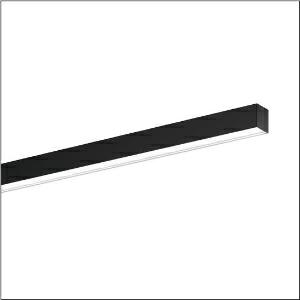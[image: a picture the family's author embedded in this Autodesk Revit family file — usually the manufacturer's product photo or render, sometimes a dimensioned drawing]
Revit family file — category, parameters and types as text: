
# Revit family: silica_r__21_51mx23tbt5b_7df7
name_source: partatom
category: Lighting Fixtures
units: mm (PartAtom-declared; Revit-internal decimal feet)

## family parameters
Cut with Voids When Loaded = No
Host = Face
Light Source = No
Part Type = Normal
Room Calculation Point = No
Round Connector Dimension = Use Diameter
Shared = No

## types (1)
- --- (1 x LED, 4030 lm, 40.5 W, 6500K)
    Apparent Load = 41 VA
    CIE Flux Codes = 78 96 99 100 100
    Color Rendering = 80
    Color Temperature = 6500K
    Default Elevation = 1800 mm
    Description = Silica® 21, office luminaire, primary optical cover: prismatic diffuser, of PMMA, CAT 2 (L<= 3000cd/m²), light emission: direct distribution, primary light characteristic: symmetric, installation type: surface-mounted, LED, rated luminous flux: 4.030lm, luminous efficacy: 95lm/W, light colour: 8tw, colour temperature: 2700..6500K, control gear: ECG DALI, with terminal, 3+2-pole, max. 2.5mm², mains connection: 220..240V, AC, 50/60Hz, rated input power: 42.6W, luminaire housing, of aluminium, jet black (RAL 9005), length: 1.504mm, width: 53mm, height: 53mm, protection rating (complete): IP20, insulation class (complete): insulation class I (protective earthing), certification: CE, permissible operating ambient temperature: 0..+35°C, standard: EN 50419, packaging unit: 1 piece
    Height = 0 mm  [stored 0 ft]
    Lamp = 1 x LED
    Lamp Light Flux = 4030 lm
    Lamp Power = 40.5 W
    Lamp count = 1
    Length = 1504 mm
    Luminous efficacy = 100 lm/W
    Manufacturer = Siteco
    ModVariant = No
    Model = 51MX23TBT5B
    Mounting Place = Ceiling
    Mounting Type = Recessed
    Number of Poles = 1
    OnlyDefault = Yes
    Power Factor = 1
    Product Name = Silica® 21
    Product group = office luminaire | ceiling recessed
    ProductGroupID = 401
    Protection Class = Protection class I
    Protection Degree = IP 20
    RLX_Detail_Level = 1
    RLX_Emergency_Light_Flux = 0 lm
    RLX_Emergency_Type = 0
    RLX_Emergency_Type_DB = No
    RlxData = <blob elided: 20481 chars, md5=839f2447>
    Socket = socket
    Standby Power = 0 W
    System Light Flux = 4030 lm
    System Power = 41 W
    Type Comments = individual setting
    Type Image = l_1313584.jpg
    URL = http://relux.com
    VarID = @adj_089181
    Voltage = 0 V
    Weight = 0.00 kg
    Width = 53 mm

note: [stored X ft] marks values corroborated as IEEE doubles in the binary element streams (Revit-internal decimal feet)

## geometry (parser evidence)
native form markers: Blend x4, Sweep x13
no freeform markers — native parametric forms only
